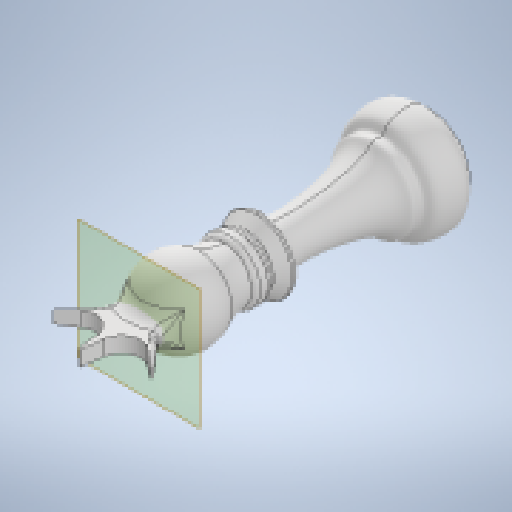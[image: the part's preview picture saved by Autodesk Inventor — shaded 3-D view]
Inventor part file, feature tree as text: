
AUTODESK INVENTOR PART (.ipt)
format: ipt  version: 2024.1 (Build 281209000, 209)  size: 711,168 bytes
history: native  units: mm
features: fillet x9, sketch x6, extrude x5, chamfer x3, projected_geometry x2, other x1, revolve x1, plane x1
ambient origin geometry x8: Origin, YZ Plane, XZ Plane, XY Plane, X Axis, Y Axis, Z Axis, Center Point
bodies: Solid1 (feature_tree)
feature tree (28):
  extrude  "Extrusion1"  Depth=10.0mm TaperAngle=0.0deg
  other  "Work Axis1"
  extrude  "Extrusion2"  Depth=14.3mm
  revolve  "Revolution1"  [1 undecoded]
  fillet  "Fillet2"  Radius=9.4mm
  chamfer  "Chamfer3"  Distance=10.36mm
  chamfer  "Chamfer4"  Distance=5.18mm
  fillet  "Fillet3"  Radius=12.3mm
  fillet  "Fillet4"  Radius=6.15mm
  fillet  "Fillet5"  Radius=2.2mm
  fillet  "Fillet9"  Radius=1.5mm
  plane  "Work Plane9"
  extrude  "Extrusion11"  Depth=1.0mm
  extrude  "Extrusion12"  Depth=1.0mm
  extrude  "Extrusion13"  Depth=1.0mm
  fillet  "Fillet10"  Radius=1.45mm
  chamfer  "Chamfer7"  Distance=1.0mm
  fillet  "Fillet11"  Radius=1.0mm
  fillet  "Fillet12"  Radius=0.6mm
  fillet  "Fillet13"  Radius=42.6mm
  sketch  "Sketch1"  dims[d0=10.0mm d1=3.0mm d2=0.0mm]
  sketch  "Sketch2"  dims[d5=360.0deg d6=14.3mm]
  sketch  "Sketch3"  dims[d7=3.0mm d8=0.0mm d74=13.55mm d81=9.4mm]
  projected_geometry  "Projected Loop1"
  sketch  "Sketch16"  dims[d82=4.7mm]
  sketch  "Sketch17"  dims[d84=10.56mm]
  sketch  "Sketch18"  dims[d85=5.28mm d87=10.36mm d88=5.18mm d89=12.3mm d90=6.15mm d91=2.2mm d92=1.5mm d93=2.03mm d98=1.0mm d99=0.1mm d100=3.17mm d101=6.108652mm d102=1.45mm d103=2.0mm d104=6.108652mm d105=1.0mm d106=1.0mm d107=0.6mm d127=42.6mm d128=10.0mm d129=1.3mm d130=1.3mm d133=2.0mm d134=0.0mm d135=2.0mm d136=0.0mm d137=10.0mm d138=1.5mm d139=2.0mm d140=45.0deg d141=6.4mm d142=2.133333mm d143=2.133333mm d144=2.133333mm d145=3.2mm d146=3.2mm d147=0.2mm d148=0.0mm d149=8.726646mm d150=3.2mm d151=0.3mm d152=2.0mm d153=0.0mm d154=3.0mm d155=1.0mm]
  projected_geometry  "Projected Loop3"
note: 1 required parameter value undecoded (feature->parameter linkage not recoverable at this tier; creation-order binding heuristic only, values carry confidence <= 0.55)
